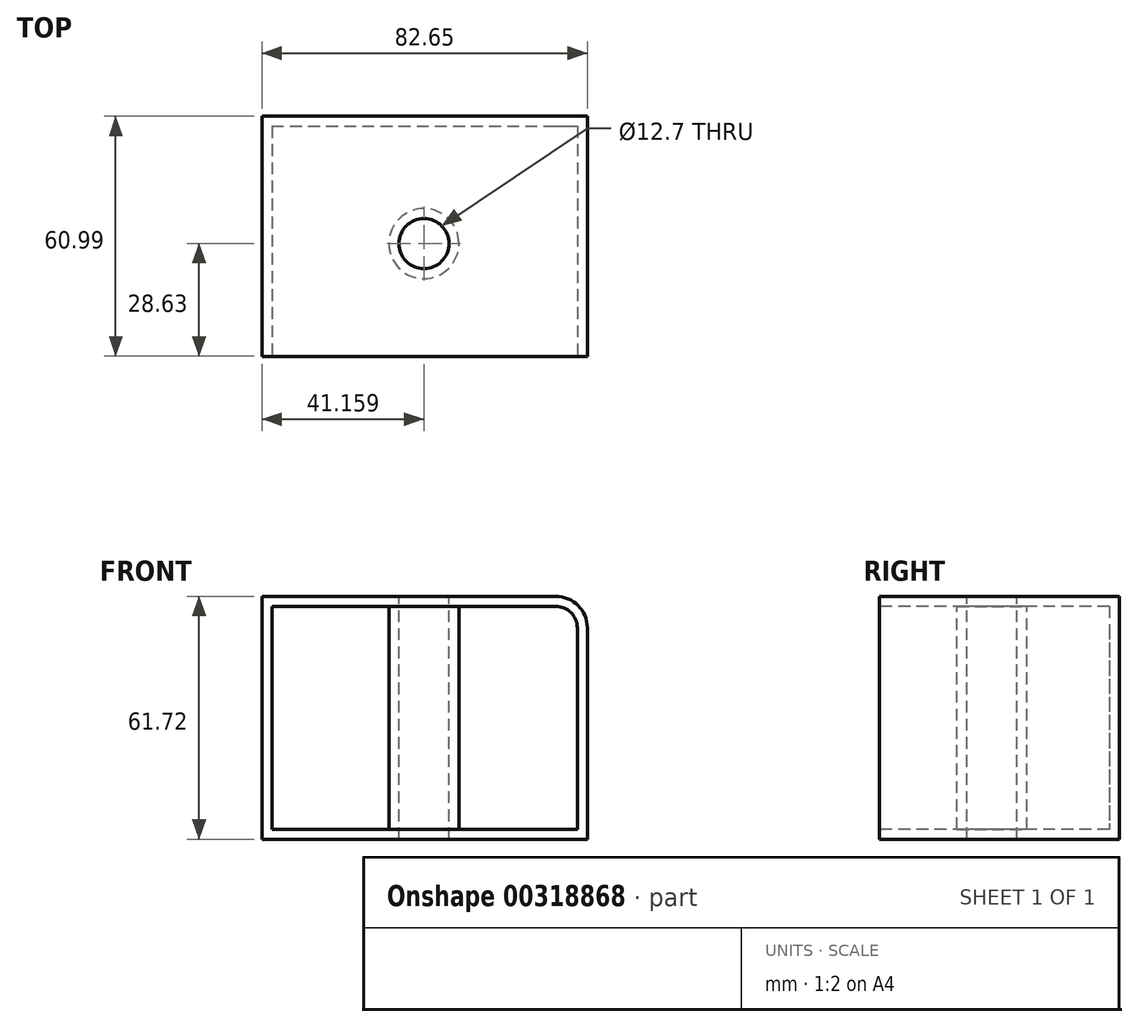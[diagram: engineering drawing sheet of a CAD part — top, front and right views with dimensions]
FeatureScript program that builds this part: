
annotation { "Feature Type Name" : "Feature", "Feature Type Description" : "" }
export const myFeature = defineFeature(function(context is Context, id is Id, definition is map)
    precondition{}
    {
        {
            var Q0;
            Q0=qCreatedBy(makeId("Top.planeOp"),FACE);
            var sketch = newSketch(context, id + "F0", { "sketchPlane" : qUnion([Q0])});
            skLineSegment(sketch, "E0.bottom", {"start": v(0, 0) * mm, "end": v(82.65, 0) * mm});
            skLineSegment(sketch, "E0.top", {"start": v(0, -61) * mm, "end": v(82.65, -61) * mm});
            skLineSegment(sketch, "E0.left", {"start": v(0, 0) * mm, "end": v(0, -61) * mm});
            skLineSegment(sketch, "E0.right", {"start": v(82.65, 0) * mm, "end": v(82.65, -61) * mm});
            skSolve(sketch);
        }
        {
            var Q0;
            Q0 = qSketchRegion(id + "F0", true);
            var Q1;
            Q1=makeQuery(id+"F0.imprint","IMPRINT",FACE,{"disambiguationData":[TD([[makeQuery(id+"F0.imprint","IMPRINT",EDGE,{"derivedFrom":sQuery(id+"F0.wireOp",EDGE,"E0.bottom")}),-1.0]])]});
            extrude(context, id + "F1", {"entities" : qUnion([Q0, Q1]), "depth" : 61.72 * mm});
        }
        {
            var Q0;
            Q0=makeQuery(id+"F1.opExtrude","CAP_EDGE",EDGE,{"disambiguationData":[OSD([sQuery(id+"F0.wireOp",EDGE,"E0.right")])],"isStart":false});
            fillet(context, id + "F2", {"entities" : qUnion([Q0]), "radius" : 7.97 * mm, "tangentPropagation" : true, "allowEdgeOverflow" : false});
        }
        {
            var Q0;
            Q0=makeQuery(id+"F1.opExtrude","CAP_FACE",FACE,{"disambiguationData":[OSD([sQuery(id+"F0.wireOp",EDGE,"E0.bottom"),sQuery(id+"F0.wireOp",EDGE,"E0.top"),sQuery(id+"F0.wireOp",EDGE,"E0.left"),sQuery(id+"F0.wireOp",EDGE,"E0.right")])],"isStart":false});
            var sketch = newSketch(context, id + "F3", { "sketchPlane" : qUnion([Q0])});
            skPoint(sketch, "E1", {"position": v(41.16, -32.36) * mm});
            skSolve(sketch);
        }
        {
            var Q0;
            Q0=sQuery(id+"F3.wireOp",VERTEX,"E1");
            var Q1;
            Q1=makeQuery(id+"F1.opExtrude","SWEPT_BODY",BODY,{"disambiguationData":[OSD([sQuery(id+"F0.wireOp",EDGE,"E0.bottom"),sQuery(id+"F0.wireOp",EDGE,"E0.top"),sQuery(id+"F0.wireOp",EDGE,"E0.left"),sQuery(id+"F0.wireOp",EDGE,"E0.right")])]});
            hole(context, id + "F4", {"style" : HoleStyle.SIMPLE, "endStyle" : HoleEndStyle.THROUGH, "holeDiameter" : 12.7 * mm, "tappedDepth" : 12.7 * mm, "tapClearance" : 3, "locations" : qUnion([Q0]), "scope" : qUnion([Q1])});
        }
        {
            var Q0;
            Q0=makeQuery(id+"F1.opExtrude","SWEPT_FACE",FACE,{"disambiguationData":[OSD([sQuery(id+"F0.wireOp",EDGE,"E0.top")])]});
            shell(context, id + "F5", {"entities" : qUnion([Q0]), "thickness" : 2.54 * mm});
        }
    });
